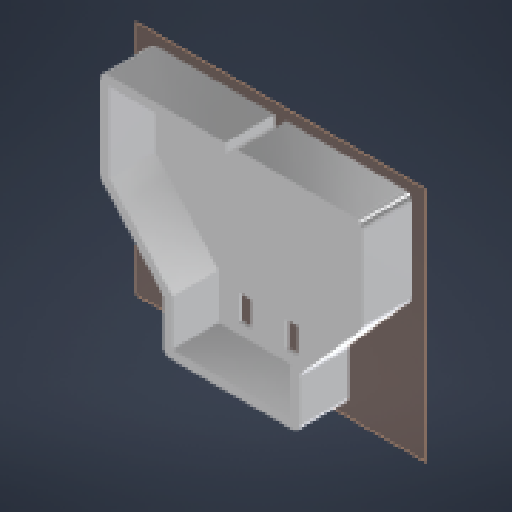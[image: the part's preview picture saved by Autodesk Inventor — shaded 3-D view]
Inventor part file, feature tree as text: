
AUTODESK INVENTOR PART (.ipt)
format: ipt  version: 2023 (Build 270158000, 158)  size: 206,848 bytes
history: native  units: in
note: dims shown in document units (in); Inventor stores cm internally (conversion verified against a paired STEP export)
features: extrude x4, reference x4, sketch x3, plane x1, fillet x1, other x1
ambient origin geometry x8: Origin, YZ Plane, XZ Plane, XY Plane, X Axis, Y Axis, Z Axis, Center Point
bodies: Solid1 (feature_tree)
feature tree (14):
  plane  "Work Plane1"
  sketch  "Sketch1"  dims[d1=1.6356in d2=0.778in]
  extrude  "Extrusion1"  Depth=0.778in
  extrude  "Extrusion2"  Depth=0.79in
  extrude  "Extrusion3"  Depth=0.02in
  fillet  "Fillet1"  Radius=1.315in
  extrude  "Extrusion4"  Depth=0.225in
  sketch  "Sketch2"  dims[d3=0.778in d6=0.79in]
  sketch  "Sketch4"  dims[d7=0.9503in d8=0.9503in d9=1.315in d10=0.225in d11=1.0087in d12=0.0625in d13=0.33in d14=0.0in d15=0.02in d16=0.0in d17=0.0in d18=0.0in d19=0.05in d30=0.3in d31=1.0in d32=0.0in d33=0.02in d34=0.02in d35=-0.2in]
  reference  "Reference1"
  reference  "Reference2"
  reference  "Reference3"
  reference  "Reference4"
  other  "kraken-power-adapter.iam"
